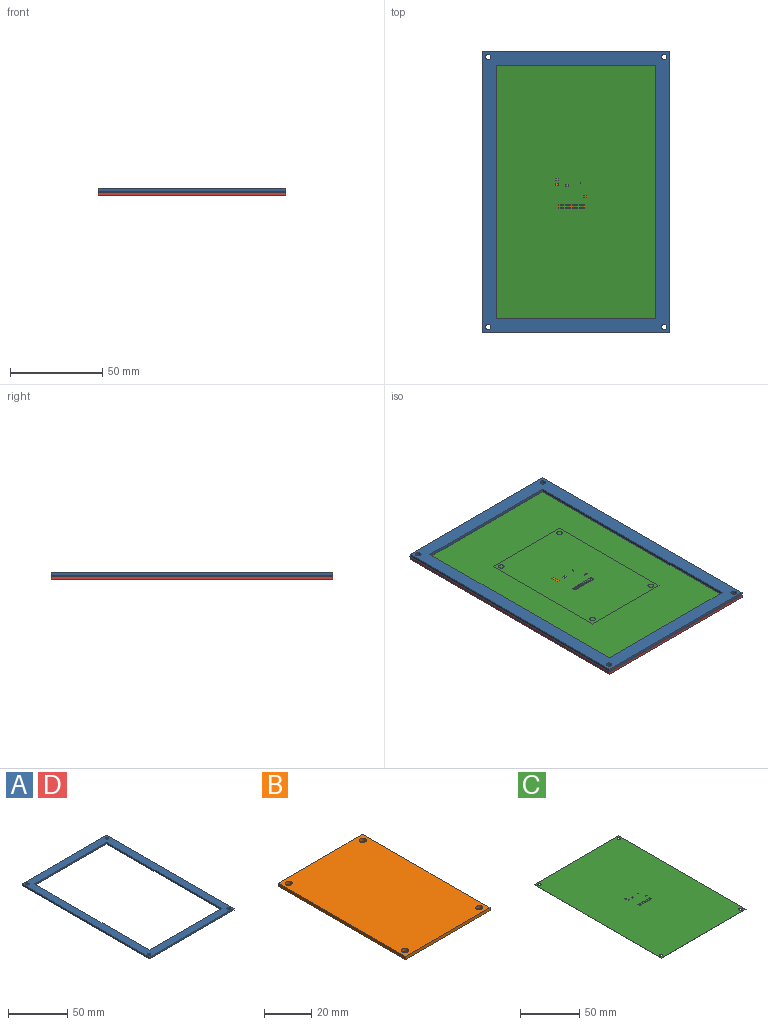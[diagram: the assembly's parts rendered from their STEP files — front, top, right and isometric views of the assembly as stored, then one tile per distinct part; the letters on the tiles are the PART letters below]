
ASSEMBLY  parts=4 mates=3
PART A: 14 faces, bbox 101.6x152.4x1.6 mm
  f0: plane 101.6x1.6mm, normal (0,1,0), area 162.6mm2, adj f1,f11,f12,f13
  f1: plane 152.4x1.6mm, normal (-1,0,0), area 243.8mm2, adj f0,f2,f12,f13
  f2: plane 101.6x1.6mm, normal (0,-1,0), area 162.6mm2, adj f1,f11,f12,f13
  f3: plane 137.16x1.6mm, normal (1,0,0), area 219.5mm2, adj f4,f6,f12,f13
  f4: plane 86.36x1.6mm, normal (0,-1,0), area 138.2mm2, adj f3,f5,f12,f13
  f5: plane 137.16x1.6mm, normal (-1,0,0), area 219.5mm2, adj f4,f6,f12,f13
  f6: plane 86.36x1.6mm, normal (0,1,0), area 138.2mm2, adj f3,f5,f12,f13
  f7: cylinder r=1.5mm len=3mm, axis (0,0,-1), area 15.1mm2, adj f12,f13
  f8: cylinder r=1.5mm len=3mm, axis (0,0,-1), area 15.1mm2, adj f12,f13
  f9: cylinder r=1.5mm len=3mm, axis (0,0,-1), area 15.1mm2, adj f12,f13
  f10: cylinder r=1.5mm len=3mm, axis (0,0,-1), area 15.1mm2, adj f12,f13
  f11: plane 152.4x1.6mm, normal (1,0,0), area 243.8mm2, adj f0,f2,f12,f13
  f12: plane 152.4x101.6mm, normal (0,0,1), area 3610.4mm2, adj f0,f1,f2,f3,f4,f5,f6,f7
  f13: plane 152.4x101.6mm, normal (0,0,-1), area 3610.4mm2, adj f0,f1,f2,f3,f4,f5,f6,f7
PART B: 10 faces, bbox 50.8x76.2x1.6 mm
  f0: plane 50.8x1.6mm, normal (0,1,0), area 81.3mm2, adj f1,f7,f8,f9
  f1: plane 76.2x1.6mm, normal (-1,0,0), area 121.9mm2, adj f0,f2,f8,f9
  f2: plane 50.8x1.6mm, normal (0,-1,0), area 81.3mm2, adj f1,f7,f8,f9
  f3: cylinder r=1.5mm len=3mm, axis (0,0,-1), area 15.1mm2, adj f8,f9
  f4: cylinder r=1.5mm len=3mm, axis (0,0,-1), area 15.1mm2, adj f8,f9
  f5: cylinder r=1.5mm len=3mm, axis (0,0,-1), area 15.1mm2, adj f8,f9
  f6: cylinder r=1.5mm len=3mm, axis (0,0,-1), area 15.1mm2, adj f8,f9
  f7: plane 76.2x1.6mm, normal (1,0,0), area 121.9mm2, adj f0,f2,f8,f9
  f8: plane 76.2x50.8mm, normal (0,0,1), area 3842.7mm2, adj f0,f1,f2,f3,f4,f5,f6,f7
  f9: plane 76.2x50.8mm, normal (0,0,-1), area 3842.7mm2, adj f0,f1,f2,f3,f4,f5,f6,f7
PART C: 82 faces, bbox 101.6x152.4x0.1 mm
  f0: plane 101.6x0.12mm, normal (0,1,0), area 12.2mm2, adj f1,f79,f80,f81
  f1: plane 152.4x0.12mm, normal (-1,0,0), area 18.3mm2, adj f0,f2,f80,f81
  f2: plane 101.6x0.12mm, normal (0,-1,0), area 12.2mm2, adj f1,f79,f80,f81
  f3: plane 1.01x0.12mm, normal (1,0,0), area 0.1mm2, adj f4,f57,f80,f81
  f4: plane 1.45x0.12mm, normal (0,-1,0), area 0.2mm2, adj f3,f5,f80,f81
  f5: plane 1.01x0.12mm, normal (-1,0,0), area 0.1mm2, adj f4,f57,f80,f81
  f6: plane 1.34x0.12mm, normal (1,0,0), area 0.2mm2, adj f7,f58,f80,f81
  f7: plane 1.45x0.12mm, normal (0,-1,0), area 0.2mm2, adj f6,f8,f80,f81
  f8: plane 1.34x0.12mm, normal (-1,0,0), area 0.2mm2, adj f7,f58,f80,f81
  f9: plane 1.23x0.12mm, normal (1,0,0), area 0.1mm2, adj f10,f59,f80,f81
  f10: plane 1.56x0.12mm, normal (0,-1,0), area 0.2mm2, adj f9,f11,f80,f81
  f11: plane 1.23x0.12mm, normal (-1,0,0), area 0.1mm2, adj f10,f59,f80,f81
  f12: plane 0.78x0.12mm, normal (1,0,0), area 0.1mm2, adj f13,f60,f80,f81
  f13: plane 0.34x0.12mm, normal (0,-1,0), area 0mm2, adj f12,f14,f80,f81
  f14: plane 0.78x0.12mm, normal (-1,0,0), area 0.1mm2, adj f13,f60,f80,f81
  f15: plane 0.67x0.12mm, normal (1,0,0), area 0.1mm2, adj f16,f61,f80,f81
  f16: plane 0.34x0.12mm, normal (0,-1,0), area 0mm2, adj f15,f17,f80,f81
  f17: plane 0.67x0.12mm, normal (-1,0,0), area 0.1mm2, adj f16,f61,f80,f81
  f18: plane 0.89x0.12mm, normal (1,0,0), area 0.1mm2, adj f19,f62,f80,f81
  f19: plane 0.34x0.12mm, normal (0,-1,0), area 0mm2, adj f18,f20,f80,f81
  f20: plane 0.89x0.12mm, normal (-1,0,0), area 0.1mm2, adj f19,f62,f80,f81
  f21: plane 1.9x0.12mm, normal (1,0,0), area 0.2mm2, adj f22,f63,f80,f81
  f22: plane 0.45x0.12mm, normal (0,-1,0), area 0.1mm2, adj f21,f23,f80,f81
  f23: plane 1.9x0.12mm, normal (-1,0,0), area 0.2mm2, adj f22,f63,f80,f81
  f24: plane 1.9x0.12mm, normal (1,0,0), area 0.2mm2, adj f25,f68,f80,f81
  f25: plane 0.45x0.12mm, normal (0,-1,0), area 0.1mm2, adj f24,f26,f80,f81
  f26: plane 1.9x0.12mm, normal (-1,0,0), area 0.2mm2, adj f25,f68,f80,f81
  f27: plane 1.9x0.12mm, normal (1,0,0), area 0.2mm2, adj f28,f69,f80,f81
  f28: plane 0.45x0.12mm, normal (0,-1,0), area 0.1mm2, adj f27,f29,f80,f81
  f29: plane 1.9x0.12mm, normal (-1,0,0), area 0.2mm2, adj f28,f69,f80,f81
  f30: plane 1.9x0.12mm, normal (1,0,0), area 0.2mm2, adj f31,f70,f80,f81
  f31: plane 0.45x0.12mm, normal (0,-1,0), area 0.1mm2, adj f30,f32,f80,f81
  f32: plane 1.9x0.12mm, normal (-1,0,0), area 0.2mm2, adj f31,f70,f80,f81
  f33: plane 1.9x0.12mm, normal (1,0,0), area 0.2mm2, adj f34,f71,f80,f81
  f34: plane 0.45x0.12mm, normal (0,-1,0), area 0.1mm2, adj f33,f35,f80,f81
  f35: plane 1.9x0.12mm, normal (-1,0,0), area 0.2mm2, adj f34,f71,f80,f81
  f36: plane 1.9x0.12mm, normal (1,0,0), area 0.2mm2, adj f37,f72,f80,f81
  f37: plane 0.45x0.12mm, normal (0,-1,0), area 0.1mm2, adj f36,f38,f80,f81
  f38: plane 1.9x0.12mm, normal (-1,0,0), area 0.2mm2, adj f37,f72,f80,f81
  f39: plane 1.9x0.12mm, normal (1,0,0), area 0.2mm2, adj f40,f73,f80,f81
  f40: plane 0.45x0.12mm, normal (0,-1,0), area 0.1mm2, adj f39,f41,f80,f81
  f41: plane 1.9x0.12mm, normal (-1,0,0), area 0.2mm2, adj f40,f73,f80,f81
  f42: plane 1.9x0.12mm, normal (1,0,0), area 0.2mm2, adj f43,f74,f80,f81
  f43: plane 0.45x0.12mm, normal (0,-1,0), area 0.1mm2, adj f42,f44,f80,f81
  f44: plane 1.9x0.12mm, normal (-1,0,0), area 0.2mm2, adj f43,f74,f80,f81
  f45: plane 1.9x0.12mm, normal (1,0,0), area 0.2mm2, adj f46,f75,f80,f81
  f46: plane 0.45x0.12mm, normal (0,-1,0), area 0.1mm2, adj f45,f47,f80,f81
  f47: plane 1.9x0.12mm, normal (-1,0,0), area 0.2mm2, adj f46,f75,f80,f81
  f48: plane 1.9x0.12mm, normal (1,0,0), area 0.2mm2, adj f49,f76,f80,f81
  f49: plane 0.45x0.12mm, normal (0,-1,0), area 0.1mm2, adj f48,f50,f80,f81
  f50: plane 1.9x0.12mm, normal (-1,0,0), area 0.2mm2, adj f49,f76,f80,f81
  f51: plane 1.9x0.12mm, normal (1,0,0), area 0.2mm2, adj f52,f77,f80,f81
  f52: plane 0.45x0.12mm, normal (0,-1,0), area 0.1mm2, adj f51,f53,f80,f81
  f53: plane 1.9x0.12mm, normal (-1,0,0), area 0.2mm2, adj f52,f77,f80,f81
  f54: plane 1.9x0.12mm, normal (1,0,0), area 0.2mm2, adj f55,f78,f80,f81
  f55: plane 0.45x0.12mm, normal (0,-1,0), area 0.1mm2, adj f54,f56,f80,f81
  f56: plane 1.9x0.12mm, normal (-1,0,0), area 0.2mm2, adj f55,f78,f80,f81
  f57: plane 1.45x0.12mm, normal (0,1,0), area 0.2mm2, adj f3,f5,f80,f81
  f58: plane 1.45x0.12mm, normal (0,1,0), area 0.2mm2, adj f6,f8,f80,f81
  f59: plane 1.56x0.12mm, normal (0,1,0), area 0.2mm2, adj f9,f11,f80,f81
  f60: plane 0.34x0.12mm, normal (0,1,0), area 0mm2, adj f12,f14,f80,f81
  f61: plane 0.34x0.12mm, normal (0,1,0), area 0mm2, adj f15,f17,f80,f81
  f62: plane 0.34x0.12mm, normal (0,1,0), area 0mm2, adj f18,f20,f80,f81
  f63: plane 0.45x0.12mm, normal (0,1,0), area 0.1mm2, adj f21,f23,f80,f81
  f64: cylinder r=1.5mm len=3mm, axis (0,0,-1), area 1.1mm2, adj f80,f81
  f65: cylinder r=1.5mm len=3mm, axis (0,0,-1), area 1.1mm2, adj f80,f81
  f66: cylinder r=1.5mm len=3mm, axis (0,0,-1), area 1.1mm2, adj f80,f81
  f67: cylinder r=1.5mm len=3mm, axis (0,0,-1), area 1.1mm2, adj f80,f81
  f68: plane 0.45x0.12mm, normal (0,1,0), area 0.1mm2, adj f24,f26,f80,f81
  f69: plane 0.45x0.12mm, normal (0,1,0), area 0.1mm2, adj f27,f29,f80,f81
  f70: plane 0.45x0.12mm, normal (0,1,0), area 0.1mm2, adj f30,f32,f80,f81
  f71: plane 0.45x0.12mm, normal (0,1,0), area 0.1mm2, adj f33,f35,f80,f81
  f72: plane 0.45x0.12mm, normal (0,1,0), area 0.1mm2, adj f36,f38,f80,f81
  f73: plane 0.45x0.12mm, normal (0,1,0), area 0.1mm2, adj f39,f41,f80,f81
  f74: plane 0.45x0.12mm, normal (0,1,0), area 0.1mm2, adj f42,f44,f80,f81
  f75: plane 0.45x0.12mm, normal (0,1,0), area 0.1mm2, adj f45,f47,f80,f81
  f76: plane 0.45x0.12mm, normal (0,1,0), area 0.1mm2, adj f48,f50,f80,f81
  f77: plane 0.45x0.12mm, normal (0,1,0), area 0.1mm2, adj f51,f53,f80,f81
  f78: plane 0.45x0.12mm, normal (0,1,0), area 0.1mm2, adj f54,f56,f80,f81
  f79: plane 152.4x0.12mm, normal (1,0,0), area 18.3mm2, adj f0,f2,f80,f81
  f80: plane 152.4x101.6mm, normal (0,0,1), area 15439.3mm2, adj f0,f1,f2,f3,f4,f5,f6,f7
  f81: plane 152.4x101.6mm, normal (0,0,-1), area 15439.3mm2, adj f0,f1,f2,f3,f4,f5,f6,f7
PART D: same geometry as A
PLACE A t=(29.11,-13.5,-10.38)mm
PLACE B t=(29.11,-13.49,-12.1)mm
PLACE C t=(29.11,-13.5,-10.5)mm
PLACE D t=(29.11,-13.5,-12.1)mm
MATE fastened C.f80 <-> A.f13  axis (0,0,1) through (-21.69,-89.7,-10.38)mm
MATE fastened C.f81 <-> B.f8  axis (0,0,-1) through (29.11,-13.49,-10.5)mm
MATE fastened D.f12 <-> C.f81  axis (0,0,1) through (79.91,-89.7,-10.5)mm
